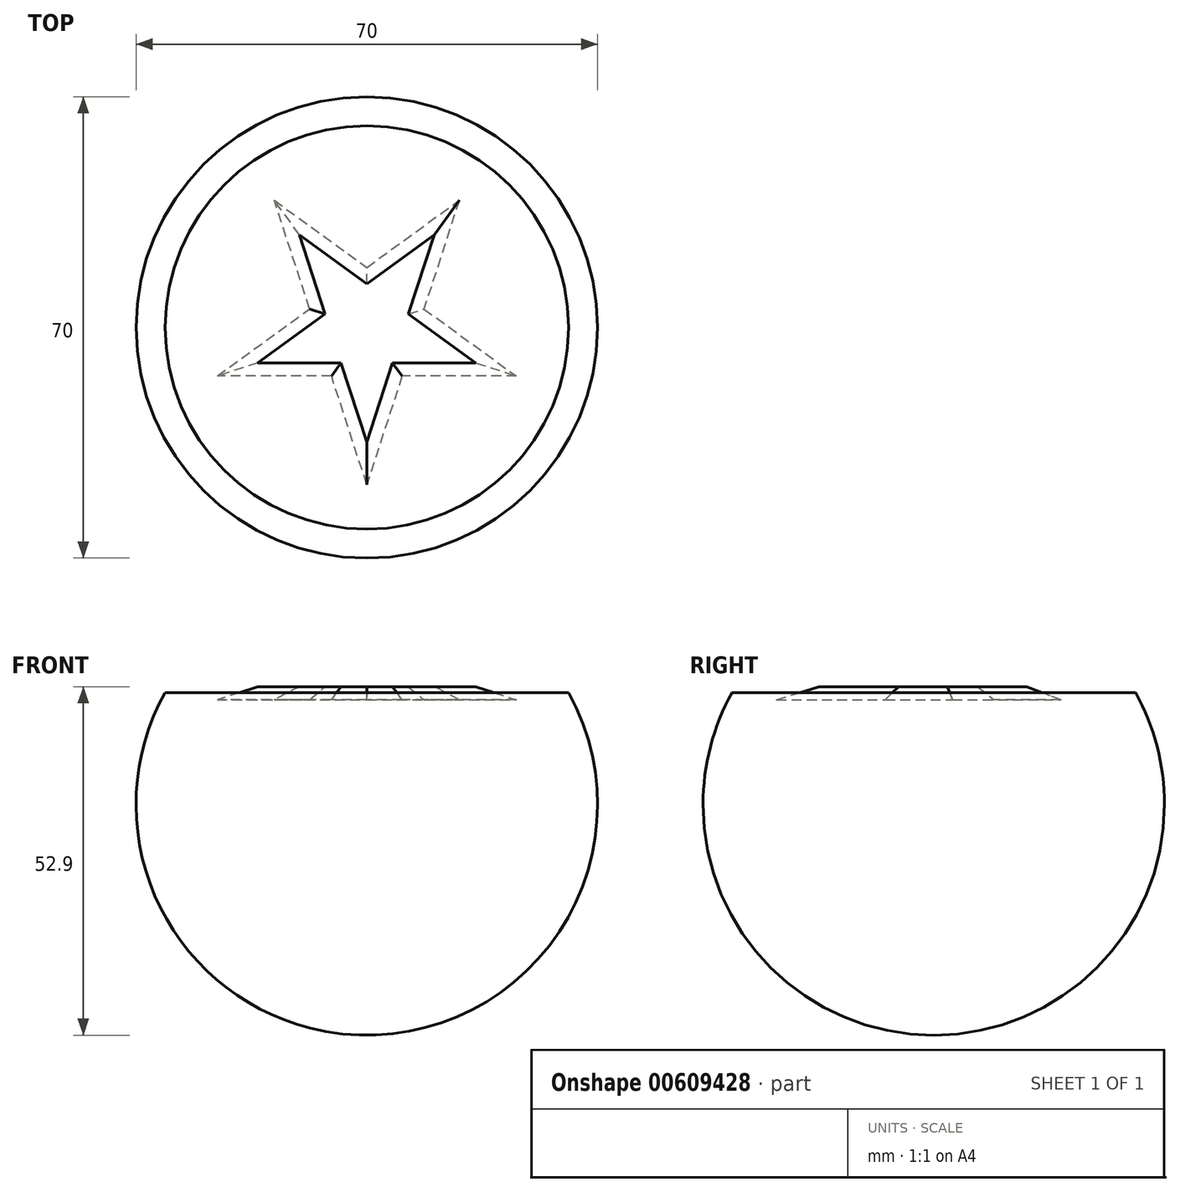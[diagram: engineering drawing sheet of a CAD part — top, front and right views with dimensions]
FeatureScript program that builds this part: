
annotation { "Feature Type Name" : "Feature", "Feature Type Description" : "" }
export const myFeature = defineFeature(function(context is Context, id is Id, definition is map)
    precondition{}
    {
        {
            var Q0;
            Q0=qCreatedBy(makeId("Top.planeOp"),FACE);
            cPlane(context, id + "F0", {"entities" : qUnion([Q0]), "cplaneType" : CPlaneType.OFFSET, "offset" : 17 * mm, "oppositeDirection" : true, "width" : 150 * mm, "height" : 150 * mm});
        }
        {
            var Q0;
            Q0=qCreatedBy(id+"F0.planeOp",FACE);
            var sketch = newSketch(context, id + "F1", { "sketchPlane" : qUnion([Q0])});
            skArc(sketch, "E0", {"start": v(0, -35) * mm, "mid": v(35, 0) * mm, "end": v(0, 35) * mm});
            skLineSegment(sketch, "E1", {"start": v(0, -57.94) * mm, "end": v(0, 63.91) * mm});
            skSolve(sketch);
        }
        {
            var Q0;
            Q0 = qSketchRegion(id + "F1", true);
            var Q1;
            Q1=sQuery(id+"F1.wireOp",EDGE,"E1");
            revolve(context, id + "F2", {"entities" : qUnion([Q0]), "axis" : qUnion([Q1]), "revolveType" : RevolveType.FULL});
        }
        {
            var Q0;
            Q0=qCreatedBy(makeId("Top.planeOp"),FACE);
            var sketch = newSketch(context, id + "F3", { "sketchPlane" : qUnion([Q0])});
            skCircle(sketch, "E2", {"center": v(0, 0) * mm, "radius": 78.75 * mm});
            skSolve(sketch);
        }
        {
            var Q0;
            Q0=qCreatedBy(makeId("Top.planeOp"),FACE);
            var sketch = newSketch(context, id + "F4", { "sketchPlane" : qUnion([Q0])});
            skCircle(sketch, "E3.cCircle", {"center": v(0, 0) * mm, "radius": 29.77 * mm, "construction": true});
            skLineSegment(sketch, "E3.0", {"start": v(-21.63, 29.77) * mm, "end": v(21.63, 29.77) * mm, "construction": true});
            skLineSegment(sketch, "E3.1", {"start": v(21.63, 29.77) * mm, "end": v(35, -11.37) * mm, "construction": true});
            skLineSegment(sketch, "E3.2", {"start": v(35, -11.37) * mm, "end": v(0, -36.8) * mm, "construction": true});
            skLineSegment(sketch, "E3.3", {"start": v(0, -36.8) * mm, "end": v(-35, -11.37) * mm, "construction": true});
            skLineSegment(sketch, "E3.4", {"start": v(-35, -11.37) * mm, "end": v(-21.63, 29.77) * mm, "construction": true});
            skPoint(sketch, "E3.0.midPoint", {"position": v(0, 29.77) * mm});
            skLineSegment(sketch, "E4", {"start": v(-21.63, 29.77) * mm, "end": v(0, -36.8) * mm});
            skLineSegment(sketch, "E5", {"start": v(0, -36.8) * mm, "end": v(21.63, 29.77) * mm});
            skLineSegment(sketch, "E6", {"start": v(21.63, 29.77) * mm, "end": v(-35, -11.37) * mm});
            skLineSegment(sketch, "E7", {"start": v(-35, -11.37) * mm, "end": v(35, -11.37) * mm});
            skLineSegment(sketch, "E8", {"start": v(35, -11.37) * mm, "end": v(-21.63, 29.77) * mm});
            skSolve(sketch);
        }
        {
            var Q0;
            Q0=qSketchRegion(id+"F4",true);
            extrude(context, id + "F5", {"entities" : qUnion([Q0]), "endBound" : BoundingType.SYMMETRIC, "depth" : 4 * mm, "offsetDistance" : 25 * mm});
        }
        {
            var Q0;
            Q0=makeQuery(id+"F5.opExtrude","CAP_FACE",FACE,{"disambiguationData":[OSD([sQuery(id+"F4.wireOp",EDGE,"E4"),sQuery(id+"F4.wireOp",EDGE,"E5"),sQuery(id+"F4.wireOp",EDGE,"E6"),sQuery(id+"F4.wireOp",EDGE,"E7"),sQuery(id+"F4.wireOp",EDGE,"E8")])],"isStart":false});
            chamfer(context, id + "F6", {"entities" : qUnion([Q0]), "width" : 8 * mm, "tangentPropagation" : true});
        }
        {
            var Q0;
            Q0 = qSketchRegion(id + "F3", true);
            extrude(context, id + "F7", {"entities" : qUnion([Q0]), "operationType" : NewBodyOperationType.REMOVE, "depth" : 25 * mm, "offsetDistance" : 25 * mm});
        }
        {
            var Q0;
            Q0=makeQuery(id+"F5.opExtrude","SWEPT_BODY",BODY,{"disambiguationData":[OSD([sQuery(id+"F4.wireOp",EDGE,"E4"),sQuery(id+"F4.wireOp",EDGE,"E5"),sQuery(id+"F4.wireOp",EDGE,"E6"),sQuery(id+"F4.wireOp",EDGE,"E7"),sQuery(id+"F4.wireOp",EDGE,"E8")])]});
            transform(context, id + "F8", {"entities" : qUnion([Q0]), "transformType" : TransformType.TRANSLATION_3D, "dx" : 0 * mm, "dy" : 0 * mm, "dz" : 0.9 * mm, "makeCopy" : false});
        }
    });
